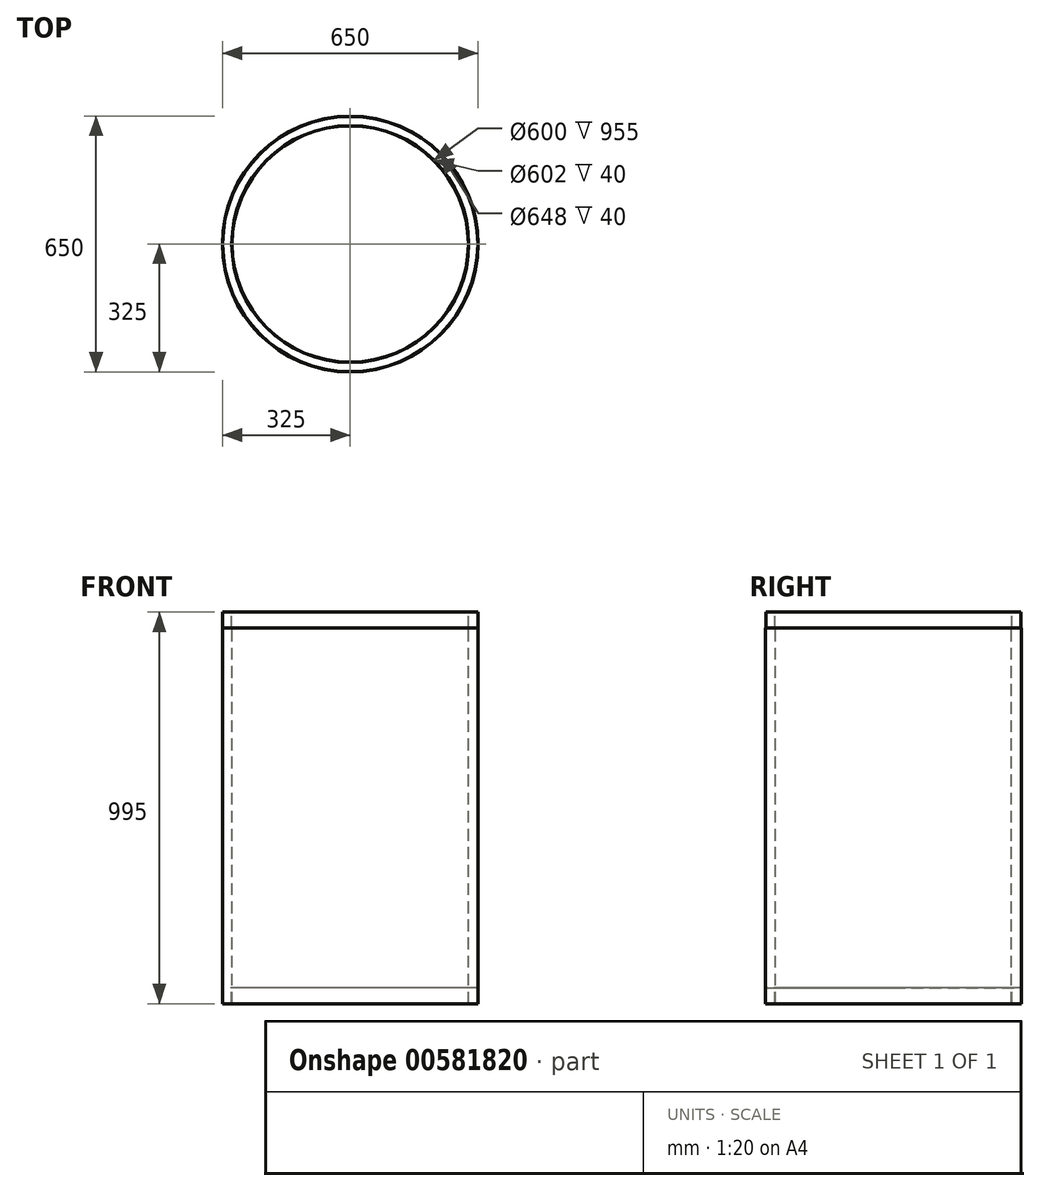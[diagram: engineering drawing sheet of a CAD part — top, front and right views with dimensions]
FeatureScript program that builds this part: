
annotation { "Feature Type Name" : "Feature", "Feature Type Description" : "" }
export const myFeature = defineFeature(function(context is Context, id is Id, definition is map)
    precondition{}
    {
        {
            var Q0;
            Q0=qCreatedBy(makeId("Front.planeOp"),FACE);
            var sketch = newSketch(context, id + "F0", { "sketchPlane" : qUnion([Q0])});
            skLineSegment(sketch, "E0", {"start": v(0, 345.75) * mm, "end": v(0, -558.03) * mm, "construction": true});
            skLineSegment(sketch, "E1", {"start": v(-300, -518.84) * mm, "end": v(-300, 436.16) * mm});
            skLineSegment(sketch, "E2", {"start": v(-300, 436.16) * mm, "end": v(-301, 436.16) * mm});
            skLineSegment(sketch, "E3", {"start": v(-301, 436.16) * mm, "end": v(-301, 476.16) * mm});
            skLineSegment(sketch, "E4", {"start": v(-301, 476.16) * mm, "end": v(-324, 476.16) * mm});
            skLineSegment(sketch, "E5", {"start": v(-324, 476.16) * mm, "end": v(-324, 436.16) * mm});
            skLineSegment(sketch, "E6", {"start": v(-324, 436.16) * mm, "end": v(-325, 436.16) * mm});
            skLineSegment(sketch, "E7", {"start": v(-325, 436.16) * mm, "end": v(-325, -518.84) * mm});
            skLineSegment(sketch, "E8", {"start": v(-325, -518.84) * mm, "end": v(-324, -518.84) * mm});
            skLineSegment(sketch, "E9", {"start": v(-324, -518.84) * mm, "end": v(-324, -478.84) * mm});
            skLineSegment(sketch, "E10", {"start": v(-324, -478.84) * mm, "end": v(-301, -478.84) * mm});
            skLineSegment(sketch, "E11", {"start": v(-301, -478.84) * mm, "end": v(-301, -518.84) * mm});
            skLineSegment(sketch, "E12", {"start": v(-301, -518.84) * mm, "end": v(-300, -518.84) * mm});
            skSolve(sketch);
        }
        {
            var Q0;
            Q0=qSketchRegion(id+"F0",true);
            var Q1;
            Q1=sQuery(id+"F0.wireOp",EDGE,"E0");
            revolve(context, id + "F1", {"entities" : qUnion([Q0]), "axis" : qUnion([Q1]), "revolveType" : RevolveType.FULL});
        }
    });
